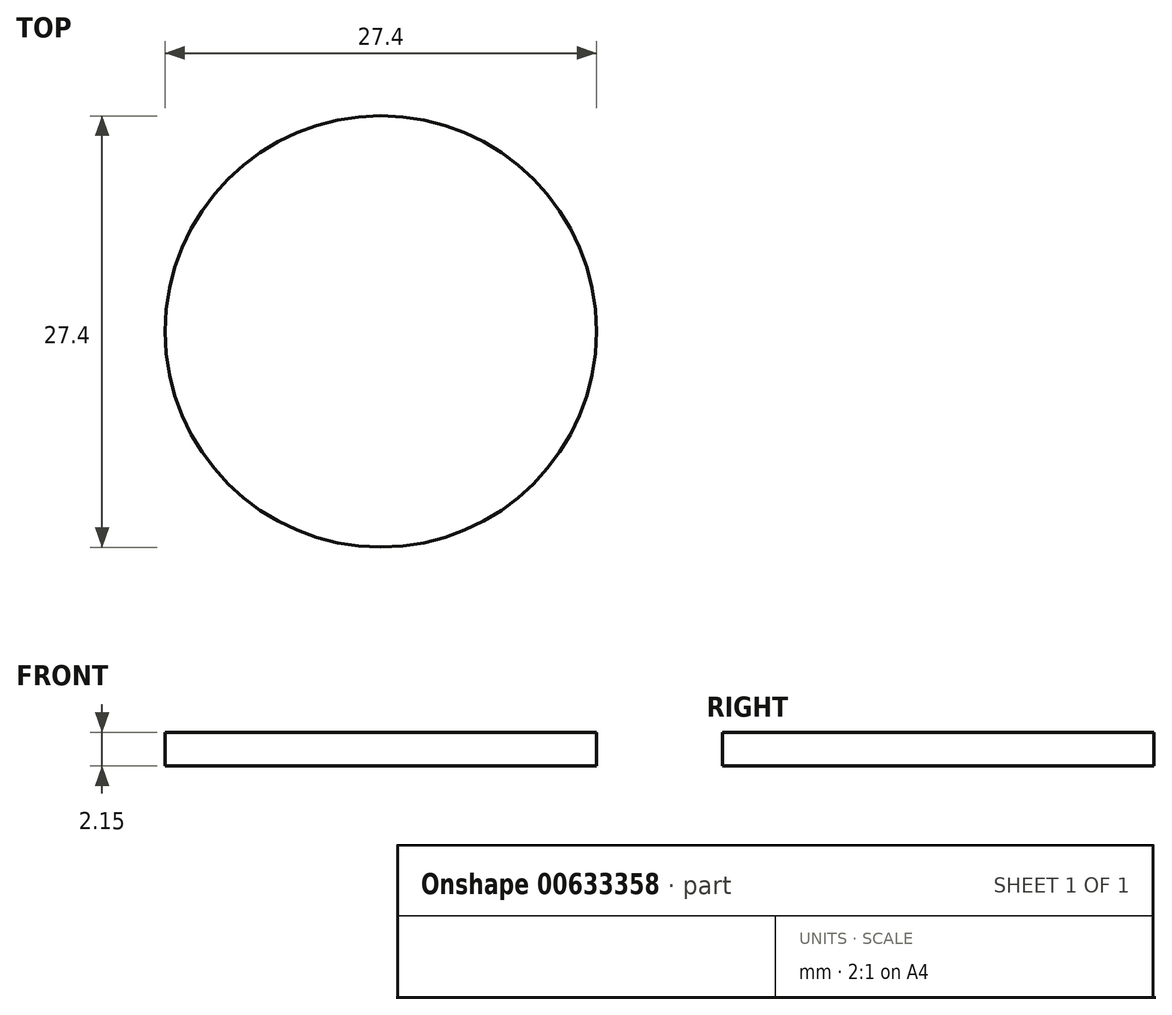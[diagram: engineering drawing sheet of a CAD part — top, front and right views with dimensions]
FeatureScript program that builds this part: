
annotation { "Feature Type Name" : "Feature", "Feature Type Description" : "" }
export const myFeature = defineFeature(function(context is Context, id is Id, definition is map)
    precondition{}
    {
        {
            var Q0;
            Q0=qCreatedBy(makeId("Top.planeOp"),FACE);
            var sketch = newSketch(context, id + "F0", { "sketchPlane" : qUnion([Q0])});
            skCircle(sketch, "E0", {"center": v(-24.35, 10.82) * mm, "radius": 13.7 * mm});
            skSolve(sketch);
        }
        {
            var Q0;
            Q0=makeQuery(id+"F0.imprint","IMPRINT",FACE,{"disambiguationData":[TD([[makeQuery(id+"F0.imprint","IMPRINT",EDGE,{"derivedFrom":sQuery(id+"F0.wireOp",EDGE,"E0")}),1.0]])]});
            extrude(context, id + "F1", {"entities" : qUnion([Q0]), "depth" : 2.15 * mm, "offsetDistance" : 25 * mm});
        }
    });
